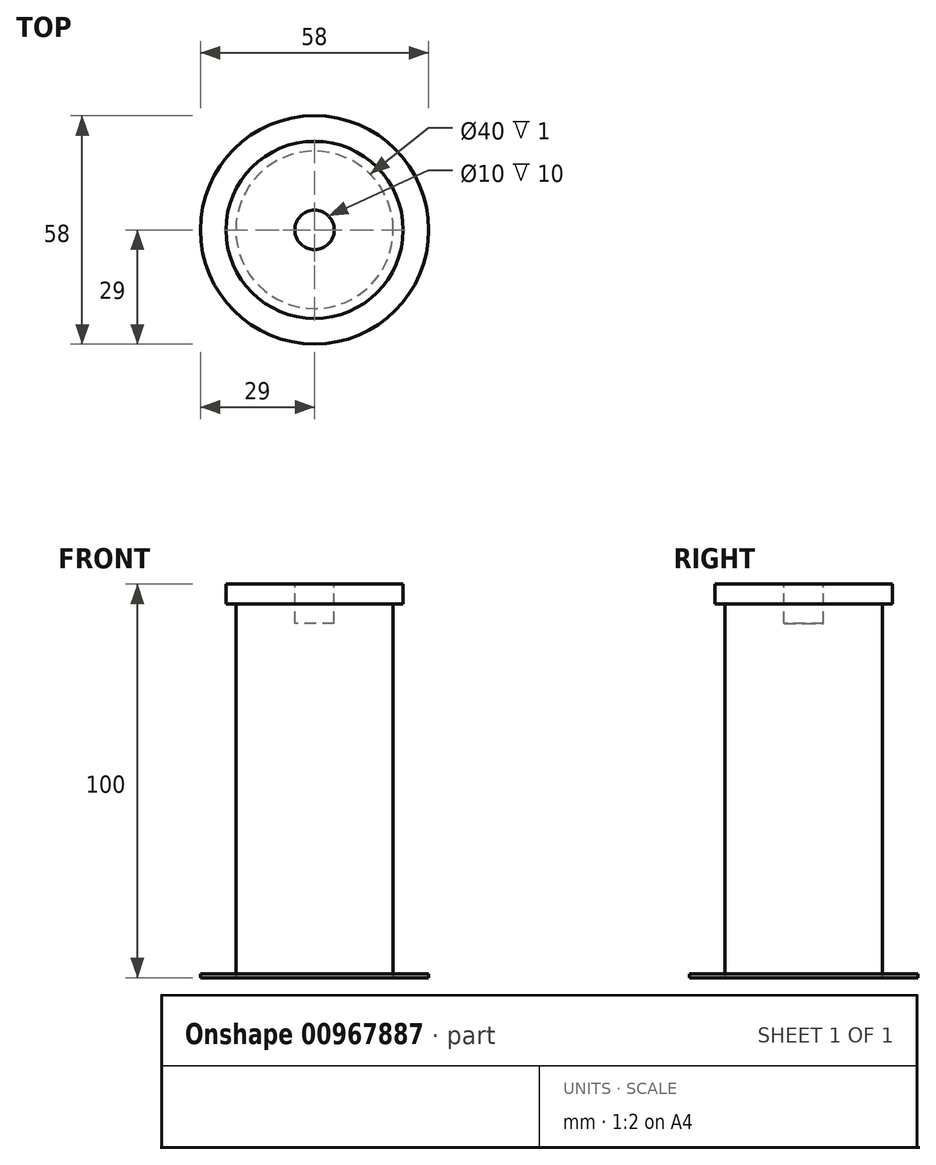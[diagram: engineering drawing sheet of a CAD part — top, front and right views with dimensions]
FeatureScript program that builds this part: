
annotation { "Feature Type Name" : "Feature", "Feature Type Description" : "" }
export const myFeature = defineFeature(function(context is Context, id is Id, definition is map)
    precondition{}
    {
        {
            var Q0;
            Q0=qCreatedBy(makeId("Top.planeOp"),FACE);
            var sketch = newSketch(context, id + "F0", { "sketchPlane" : qUnion([Q0])});
            skCircle(sketch, "E0", {"center": v(0, 0) * mm, "radius": 20 * mm});
            skCircle(sketch, "E1", {"center": v(0, 0) * mm, "radius": 29 * mm});
            skSolve(sketch);
        }
        {
            var Q0;
            Q0=makeQuery(id+"F0.imprint","IMPRINT",FACE,{"disambiguationData":[TD([[makeQuery(id+"F0.imprint","IMPRINT",EDGE,{"derivedFrom":sQuery(id+"F0.wireOp",EDGE,"E0")}),1.0]])]});
            extrude(context, id + "F1", {"entities" : qUnion([Q0]), "depth" : 100 * mm, "offsetDistance" : 25 * mm});
        }
        {
            var Q0;
            Q0=makeQuery(id+"F0.imprint","IMPRINT",FACE,{"disambiguationData":[TD([[makeQuery(id+"F0.imprint","IMPRINT",EDGE,{"derivedFrom":sQuery(id+"F0.wireOp",EDGE,"E0")}),-1.0]])]});
            extrude(context, id + "F2", {"entities" : qUnion([Q0]), "depth" : 1 * mm, "offsetDistance" : 25 * mm});
        }
        {
            var Q0;
            Q0=sQuery(id+"F0.wireOp",EDGE,"E1");
            var Q1;
            Q1=makeQuery(id+"F1.opExtrude","CAP_EDGE",EDGE,{"disambiguationData":[OSD([sQuery(id+"F0.wireOp",EDGE,"E0")])],"isStart":false});
            loft(context, id + "F3", {"bodyType" : ToolBodyType.SURFACE, "wireProfilesArray" : [{ "wireProfileEntities" : qUnion([Q0]) }, { "wireProfileEntities" : qUnion([Q1]) }]});
        }
        {
            var Q0;
            Q0=makeQuery(id+"F1.opExtrude","CAP_FACE",FACE,{"disambiguationData":[OSD([sQuery(id+"F0.wireOp",EDGE,"E0")])],"isStart":false});
            var sketch = newSketch(context, id + "F4", { "sketchPlane" : qUnion([Q0])});
            skCircle(sketch, "E2", {"center": v(0, 0) * mm, "radius": 22.5 * mm});
            skCircle(sketch, "E3", {"center": v(0, 0) * mm, "radius": 5 * mm});
            skSolve(sketch);
        }
        {
            var Q0;
            Q0=makeQuery(id+"F4.imprint","IMPRINT",FACE,{"disambiguationData":[TD([[makeQuery(id+"F4.imprint","IMPRINT",EDGE,{"derivedFrom":makeQuery(id+"F1.opExtrude","CAP_EDGE",EDGE,{"disambiguationData":[OSD([sQuery(id+"F0.wireOp",EDGE,"E0")])],"isStart":false})}),1.0]])]});
            var Q1;
            Q1=makeQuery(id+"F4.imprint","IMPRINT",FACE,{"disambiguationData":[TD([[makeQuery(id+"F4.imprint","IMPRINT",EDGE,{"derivedFrom":sQuery(id+"F4.wireOp",EDGE,"E2")}),1.0]])]});
            extrude(context, id + "F5", {"entities" : qUnion([Q0, Q1]), "operationType" : NewBodyOperationType.ADD, "oppositeDirection" : true, "depth" : 5 * mm, "offsetDistance" : 25 * mm});
        }
        {
            var Q0;
            Q0=makeQuery(id+"F4.imprint","IMPRINT",FACE,{"disambiguationData":[TD([[makeQuery(id+"F4.imprint","IMPRINT",EDGE,{"derivedFrom":sQuery(id+"F4.wireOp",EDGE,"E3")}),1.0]])]});
            extrude(context, id + "F6", {"entities" : qUnion([Q0]), "operationType" : NewBodyOperationType.REMOVE, "oppositeDirection" : true, "depth" : 10 * mm, "offsetDistance" : 25 * mm});
        }
    });
